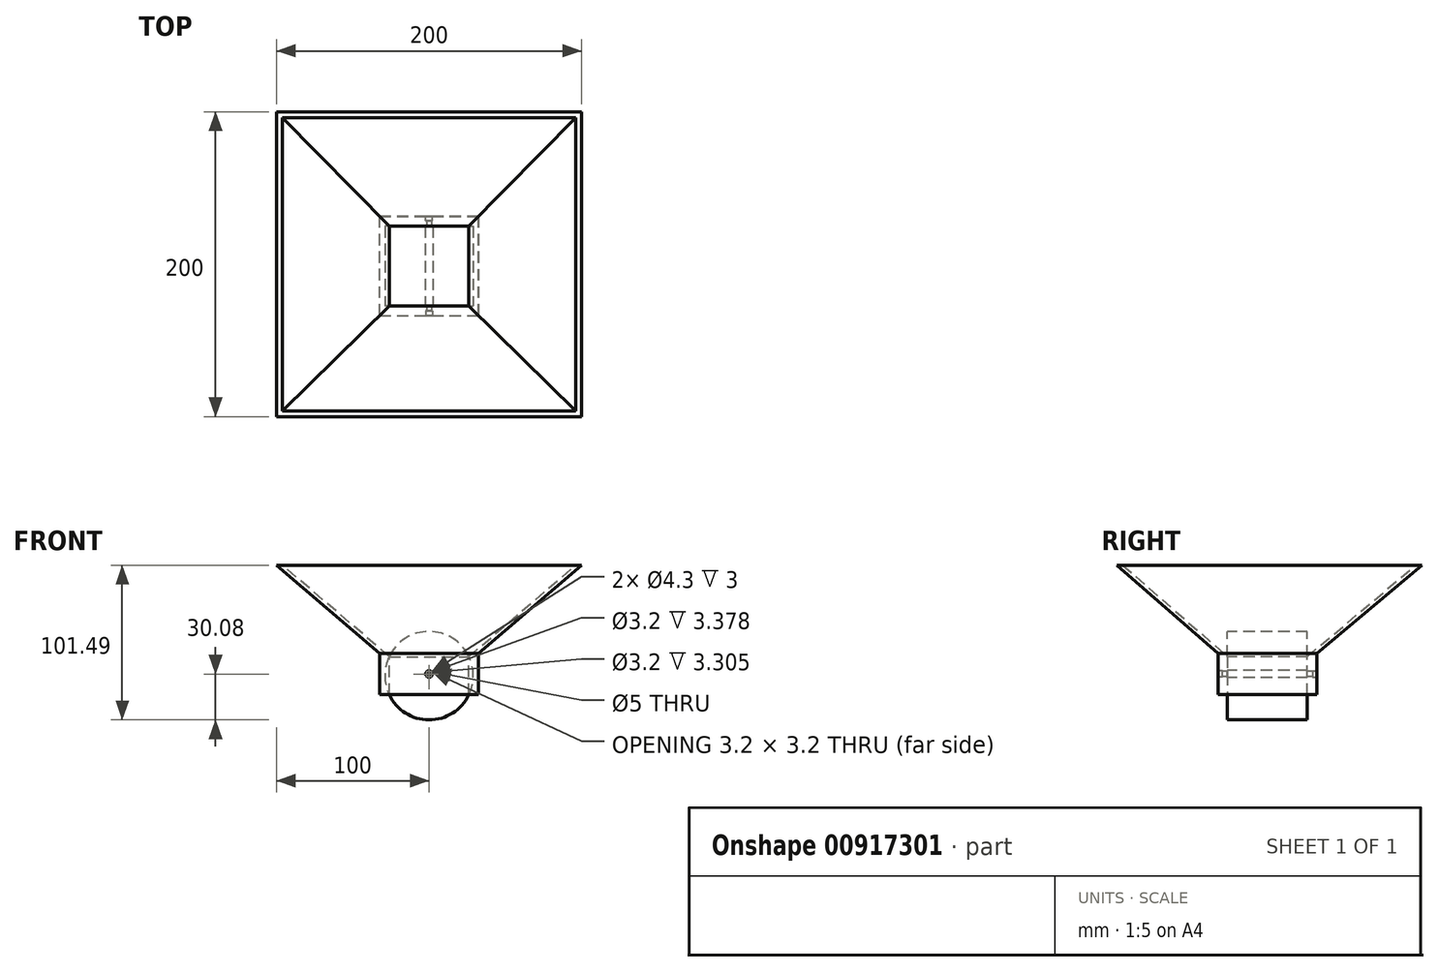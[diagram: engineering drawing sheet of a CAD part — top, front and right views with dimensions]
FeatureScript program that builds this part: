
annotation { "Feature Type Name" : "Feature", "Feature Type Description" : "" }
export const myFeature = defineFeature(function(context is Context, id is Id, definition is map)
    precondition{}
    {
        {
            assignVariable(context, id + "F0", {"name" : "top_height", "anyValue" : 60 * mm});
        }
        {
            var Q0;
            Q0=qCreatedBy(makeId("Top.planeOp"),FACE);
            var sketch = newSketch(context, id + "F1", { "sketchPlane" : qUnion([Q0])});
            skLineSegment(sketch, "E0.bottom", {"start": v(-100, 101.17) * mm, "end": v(100, 101.17) * mm});
            skLineSegment(sketch, "E0.top", {"start": v(-100, -98.83) * mm, "end": v(100, -98.83) * mm});
            skLineSegment(sketch, "E0.left", {"start": v(-100, 101.17) * mm, "end": v(-100, -98.83) * mm});
            skLineSegment(sketch, "E0.right", {"start": v(100, 101.17) * mm, "end": v(100, -98.83) * mm});
            skPoint(sketch, "E0.middle", {"position": v(0, 1.17) * mm});
            skSolve(sketch);
        }
        {
            var Q0;
            Q0=makeQuery(id+"F1.imprint","IMPRINT",FACE,{"disambiguationData":[TD([[makeQuery(id+"F1.imprint","IMPRINT",EDGE,{"derivedFrom":sQuery(id+"F1.wireOp",EDGE,"E0.bottom")}),-1.0]])]});
            cPlane(context, id + "F2", {"entities" : qUnion([Q0]), "cplaneType" : CPlaneType.OFFSET, "offset" : getVariable(context, 'top_height'), "oppositeDirection" : true, "width" : 150 * mm, "height" : 150 * mm});
        }
        {
            var Q0;
            Q0=qCreatedBy(id+"F2.planeOp",FACE);
            var sketch = newSketch(context, id + "F3", { "sketchPlane" : qUnion([Q0])});
            skLineSegment(sketch, "E1.bottom", {"start": v(30, 30) * mm, "end": v(-30, 30) * mm});
            skLineSegment(sketch, "E1.top", {"start": v(30, -30) * mm, "end": v(-30, -30) * mm});
            skLineSegment(sketch, "E1.left", {"start": v(30, 30) * mm, "end": v(30, -30) * mm});
            skLineSegment(sketch, "E1.right", {"start": v(-30, 30) * mm, "end": v(-30, -30) * mm});
            skPoint(sketch, "E1.middle", {"position": v(0, 0) * mm});
            skSolve(sketch);
        }
        {
            var Q0;
            Q0=makeQuery(id+"F1.imprint","IMPRINT",FACE,{"disambiguationData":[TD([[makeQuery(id+"F1.imprint","IMPRINT",EDGE,{"derivedFrom":sQuery(id+"F1.wireOp",EDGE,"E0.bottom")}),-1.0]])]});
            var Q1;
            Q1=makeQuery(id+"F3.imprint","IMPRINT",FACE,{"disambiguationData":[TD([[makeQuery(id+"F3.imprint","IMPRINT",EDGE,{"derivedFrom":sQuery(id+"F3.wireOp",EDGE,"E1.bottom")}),1.0]])]});
            loft(context, id + "F4", {"sheetProfilesArray" : [{ "sheetProfileEntities" : qUnion([Q0]) }, { "sheetProfileEntities" : qUnion([Q1]) }]});
        }
        {
            var Q0;
            Q0=makeQuery(id+"F4.opLoft","CAP_FACE",FACE,{"disambiguationData":[OSD([makeQuery(id+"F1.imprint","IMPRINT",FACE,{"disambiguationData":[TD([[makeQuery(id+"F1.imprint","IMPRINT",EDGE,{"derivedFrom":sQuery(id+"F1.wireOp",EDGE,"E0.bottom")}),-1.0]])]})])],"isStart":true});
            var Q1;
            Q1=makeQuery(id+"F4.opLoft","CAP_FACE",FACE,{"disambiguationData":[OSD([makeQuery(id+"F3.imprint","IMPRINT",FACE,{"disambiguationData":[TD([[makeQuery(id+"F3.imprint","IMPRINT",EDGE,{"derivedFrom":sQuery(id+"F3.wireOp",EDGE,"E1.bottom")}),1.0]])]})])],"isStart":true});
            shell(context, id + "F5", {"entities" : qUnion([Q0, Q1]), "thickness" : 2.5 * mm});
        }
        {
            var Q0;
            Q0=makeQuery(id+"F4.opLoft","CAP_FACE",FACE,{"disambiguationData":[OSD([makeQuery(id+"F3.imprint","IMPRINT",FACE,{"disambiguationData":[TD([[makeQuery(id+"F3.imprint","IMPRINT",EDGE,{"derivedFrom":sQuery(id+"F3.wireOp",EDGE,"E1.bottom")}),1.0]])]})])],"isStart":true});
            var sketch = newSketch(context, id + "F6", { "sketchPlane" : qUnion([Q0])});
            skLineSegment(sketch, "E2.bottom", {"start": v(-32.5, 32.5) * mm, "end": v(32.5, 32.5) * mm});
            skLineSegment(sketch, "E2.top", {"start": v(-32.5, -32.5) * mm, "end": v(32.5, -32.5) * mm});
            skLineSegment(sketch, "E2.left", {"start": v(-32.5, 32.5) * mm, "end": v(-32.5, -32.5) * mm});
            skLineSegment(sketch, "E2.right", {"start": v(32.5, 32.5) * mm, "end": v(32.5, -32.5) * mm});
            skPoint(sketch, "E2.middle", {"position": v(0, 0) * mm});
            skSolve(sketch);
        }
        {
            var Q0;
            Q0=makeQuery(id+"F6.imprint","IMPRINT",FACE,{"disambiguationData":[TD([[makeQuery(id+"F6.imprint","IMPRINT",EDGE,{"derivedFrom":sQuery(id+"F6.wireOp",EDGE,"E2.bottom")}),-1.0]])]});
            var Q1;
            {var subQ0=sQuery(id+"F3.wireOp",EDGE,"E1.right");var subQ1=sQuery(id+"F3.wireOp",EDGE,"E1.left");var subQ3=sQuery(id+"F3.wireOp",EDGE,"E1.bottom");Q1=makeQuery(id+"F6.imprint","IMPRINT",FACE,{"disambiguationData":[TD([[makeQuery(id+"F6.imprint","IMPRINT",EDGE,{"derivedFrom":makeQuery(id+"F4.opLoft","MID_CAP_EDGE",EDGE,{"disambiguationData":[OSD([subQ3,subQ1,subQ0])],"capPos":1.0})}),1.0]])]});}
            var Q2;
            Q2=makeQuery(id+"F4.opLoft","SWEPT_FACE",FACE,{"disambiguationData":[OSD([sQuery(id+"F1.wireOp",EDGE,"E0.bottom"),sQuery(id+"F1.wireOp",EDGE,"E0.top"),sQuery(id+"F1.wireOp",EDGE,"E0.left"),sQuery(id+"F3.wireOp",EDGE,"E1.bottom"),sQuery(id+"F3.wireOp",EDGE,"E1.top"),sQuery(id+"F3.wireOp",EDGE,"E1.right")])]});
            extrude(context, id + "F7", {"entities" : qUnion([Q0, Q1]), "operationType" : NewBodyOperationType.ADD, "depth" : 25 * mm, "offsetDistance" : 25 * mm, "hasSecondDirection" : true, "secondDirectionBound" : SecondDirectionBoundingType.UP_TO_NEXT, "secondDirectionOppositeDirection" : true, "secondDirectionDepth" : 25 * mm, "secondDirectionBoundEntityFace" : qUnion([Q2])});
        }
        {
            var Q0;
            Q0=makeQuery(id+"F7.opExtrude","SWEPT_FACE",FACE,{"disambiguationData":[OSD([sQuery(id+"F3.wireOp",EDGE,"E1.top"),sQuery(id+"F3.wireOp",EDGE,"E1.left"),sQuery(id+"F3.wireOp",EDGE,"E1.right")])]});
            var sketch = newSketch(context, id + "F8", { "sketchPlane" : qUnion([Q0])});
            skPoint(sketch, "E3", {"position": v(0, -85) * mm});
            skPoint(sketch, "E4", {"position": v(0, -60) * mm});
            skLineSegment(sketch, "E5", {"start": v(0, -85) * mm, "end": v(0, -60) * mm, "construction": true});
            skPoint(sketch, "E6", {"position": v(0, -72.5) * mm});
            skCircle(sketch, "E7", {"center": v(0, -72.5) * mm, "radius": 29 * mm});
            skSolve(sketch);
        }
        {
            var Q0;
            {var subQ1=sQuery(id+"F3.wireOp",EDGE,"E1.right");var subQ2=sQuery(id+"F3.wireOp",EDGE,"E1.left");var subQ3=sQuery(id+"F3.wireOp",EDGE,"E1.top");var subQ4=makeQuery(id+"F5.opShell","OFFSET_EDGE",EDGE,{"disambiguationData":[OSD([subQ3,subQ2,subQ1])]});var subQ5=makeQuery(id+"F7.opExtrude","CAP_EDGE",EDGE,{"disambiguationData":[OSD([subQ3,subQ2,subQ1]),TDD([makeQuery(id+"F6.imprint","IMPRINT",EDGE,{"derivedFrom":subQ4})])],"isStart":false});Q0=makeQuery(id+"F8.imprint","IMPRINT",FACE,{"disambiguationData":[TD([[makeQuery(id+"F8.imprint","IMPRINT",EDGE,{"derivedFrom":subQ5}),-1.0]])]});}
            var Q1;
            {var subQ0=sQuery(id+"F3.wireOp",EDGE,"E1.right");var subQ1=sQuery(id+"F3.wireOp",EDGE,"E1.left");var subQ2=sQuery(id+"F3.wireOp",EDGE,"E1.top");var subQ3=makeQuery(id+"F5.opShell","OFFSET_EDGE",EDGE,{"disambiguationData":[OSD([subQ2,subQ1,subQ0])]});var subQ5=makeQuery(id+"F6.imprint","IMPRINT",EDGE,{"derivedFrom":subQ3});Q1=makeQuery(id+"F8.imprint","IMPRINT",FACE,{"disambiguationData":[TD([[makeQuery(id+"F8.imprint","IMPRINT",EDGE,{"derivedFrom":makeQuery(id+"F7.opExtrude","CAP_EDGE",EDGE,{"disambiguationData":[OSD([subQ2,subQ1,subQ0]),TDD([subQ5])],"isStart":false})}),1.0]])]});}
            var Q2;
            {var subQ1=sQuery(id+"F3.wireOp",EDGE,"E1.right");var subQ2=sQuery(id+"F3.wireOp",EDGE,"E1.left");var subQ3=sQuery(id+"F3.wireOp",EDGE,"E1.top");var subQ4=makeQuery(id+"F5.opShell","OFFSET_EDGE",EDGE,{"disambiguationData":[OSD([subQ3,subQ2,subQ1])]});var subQ5=makeQuery(id+"F7.boolean.opBoolean","MERGE",EDGE,{"derivedFrom":[subQ4,makeQuery(id+"F7.opExtrude","CAP_EDGE",EDGE,{"disambiguationData":[OSD([subQ3,subQ2,subQ1]),TDD([subQ4,makeQuery(id+"F6.imprint","IMPRINT",EDGE,{"derivedFrom":subQ4})])],"isStart":false})]});Q2=makeQuery(id+"F8.imprint","IMPRINT",FACE,{"disambiguationData":[TD([[makeQuery(id+"F8.imprint","IMPRINT",EDGE,{"derivedFrom":subQ5}),1.0]])]});}
            var Q3;
            {var subQ1=sQuery(id+"F3.wireOp",EDGE,"E1.right");var subQ2=sQuery(id+"F3.wireOp",EDGE,"E1.left");var subQ3=sQuery(id+"F3.wireOp",EDGE,"E1.top");var subQ4=makeQuery(id+"F5.opShell","OFFSET_EDGE",EDGE,{"disambiguationData":[OSD([subQ3,subQ2,subQ1])]});var subQ6=sQuery(id+"F3.wireOp",EDGE,"E1.bottom");var subQ7=makeQuery(id+"F7.opExtrude","SWEPT_EDGE",EDGE,{"disambiguationData":[OSD([subQ6,subQ3,subQ2,subQ1]),TDD([makeQuery(id+"F6.imprint","INTERSECT",VERTEX,{"derivedFrom":[makeQuery(id+"F5.opShell","OFFSET_EDGE",EDGE,{"disambiguationData":[OSD([subQ6,subQ3,subQ1])]}),subQ4]})])]});Q3=makeQuery(id+"F8.imprint","IMPRINT",FACE,{"disambiguationData":[TD([[makeQuery(id+"F8.imprint","IMPRINT",EDGE,{"derivedFrom":subQ7}),-1.0]])]});}
            var Q4;
            {var subQ1=sQuery(id+"F3.wireOp",EDGE,"E1.right");var subQ2=sQuery(id+"F3.wireOp",EDGE,"E1.left");var subQ3=sQuery(id+"F3.wireOp",EDGE,"E1.top");var subQ4=makeQuery(id+"F5.opShell","OFFSET_EDGE",EDGE,{"disambiguationData":[OSD([subQ3,subQ2,subQ1])]});var subQ6=sQuery(id+"F3.wireOp",EDGE,"E1.bottom");var subQ7=makeQuery(id+"F7.opExtrude","SWEPT_EDGE",EDGE,{"disambiguationData":[OSD([subQ6,subQ3,subQ2,subQ1]),TDD([makeQuery(id+"F6.imprint","INTERSECT",VERTEX,{"derivedFrom":[makeQuery(id+"F5.opShell","OFFSET_EDGE",EDGE,{"disambiguationData":[OSD([subQ6,subQ3,subQ2])]}),subQ4]})])]});Q4=makeQuery(id+"F8.imprint","IMPRINT",FACE,{"disambiguationData":[TD([[makeQuery(id+"F8.imprint","IMPRINT",EDGE,{"derivedFrom":subQ7}),1.0]])]});}
            var Q5;
            Q5=makeQuery(id+"F7.opExtrude","SWEPT_FACE",FACE,{"disambiguationData":[OSD([sQuery(id+"F3.wireOp",EDGE,"E1.bottom"),sQuery(id+"F3.wireOp",EDGE,"E1.left"),sQuery(id+"F3.wireOp",EDGE,"E1.right")])]});
            extrude(context, id + "F9", {"entities" : qUnion([Q0, Q1, Q2, Q3, Q4]), "endBound" : BoundingType.UP_TO_SURFACE, "depth" : 25 * mm, "endBoundEntityFace" : qUnion([Q5]), "offsetDistance" : 25 * mm});
        }
        {
            var Q0;
            Q0=makeQuery(id+"F9.opExtrude","SWEPT_BODY",BODY,{"disambiguationData":[OSD([sQuery(id+"F8.wireOp",EDGE,"E7")])]});
            var Q1;
            Q1=makeQuery(id+"F4.opLoft","SWEPT_BODY",BODY,{"disambiguationData":[OSD([makeQuery(id+"F1.imprint","IMPRINT",FACE,{"disambiguationData":[TD([[makeQuery(id+"F1.imprint","IMPRINT",EDGE,{"derivedFrom":sQuery(id+"F1.wireOp",EDGE,"E0.bottom")}),-1.0]])]}),makeQuery(id+"F3.imprint","IMPRINT",FACE,{"disambiguationData":[TD([[makeQuery(id+"F3.imprint","IMPRINT",EDGE,{"derivedFrom":sQuery(id+"F3.wireOp",EDGE,"E1.bottom")}),1.0]])]})])]});
            booleanBodies(context, id + "F10", {"operationType" : BooleanOperationType.SUBTRACTION, "tools" : qUnion([Q0]), "targets" : qUnion([Q1]), "keepTools" : true});
        }
        {
            var Q0;
            Q0=makeQuery(id+"F9.opExtrude","CAP_FACE",FACE,{"disambiguationData":[OSD([sQuery(id+"F8.wireOp",EDGE,"E7")])],"isStart":true});
            var sketch = newSketch(context, id + "F11", { "sketchPlane" : qUnion([Q0])});
            skPoint(sketch, "E8", {"position": v(0, -57.82) * mm});
            skPoint(sketch, "E9", {"position": v(0, -85) * mm});
            skLineSegment(sketch, "E10", {"start": v(0, -57.82) * mm, "end": v(0, -85) * mm, "construction": true});
            skCircle(sketch, "E11", {"center": v(0, -71.41) * mm, "radius": 2.5 * mm});
            skSolve(sketch);
        }
        {
            var Q0;
            Q0=makeQuery(id+"F9.opExtrude","CAP_FACE",FACE,{"disambiguationData":[OSD([sQuery(id+"F8.wireOp",EDGE,"E7")])],"isStart":true});
            var sketch = newSketch(context, id + "F12", { "sketchPlane" : qUnion([Q0])});
            skCircle(sketch, "E12.0", {"center": v(0, -71.41) * mm, "radius": 2.5 * mm, "construction": true});
            skSolve(sketch);
        }
        {
            var Q0;
            Q0=makeQuery(id+"F11.imprint","IMPRINT",FACE,{"disambiguationData":[TD([[makeQuery(id+"F11.imprint","IMPRINT",EDGE,{"derivedFrom":sQuery(id+"F11.wireOp",EDGE,"E11")}),1.0]])]});
            extrude(context, id + "F13", {"entities" : qUnion([Q0]), "operationType" : NewBodyOperationType.REMOVE, "endBound" : BoundingType.UP_TO_NEXT, "oppositeDirection" : true, "depth" : 25 * mm, "offsetDistance" : 25 * mm});
        }
        {
            var Q0;
            Q0=makeQuery(id+"F7.opExtrude","SWEPT_FACE",FACE,{"disambiguationData":[OSD([sQuery(id+"F6.wireOp",EDGE,"E2.bottom")])]});
            var sketch = newSketch(context, id + "F14", { "sketchPlane" : qUnion([Q0])});
            skCircle(sketch, "E13.0", {"center": v(0, -71.41) * mm, "radius": 2.5 * mm, "construction": true});
            skSolve(sketch);
        }
        {
            var Q0;
            Q0=sQuery(id+"F14.wireOp",VERTEX,"E13.0.center");
            var Q1;
            Q1=makeQuery(id+"F4.opLoft","SWEPT_BODY",BODY,{"disambiguationData":[OSD([makeQuery(id+"F1.imprint","IMPRINT",FACE,{"disambiguationData":[TD([[makeQuery(id+"F1.imprint","IMPRINT",EDGE,{"derivedFrom":sQuery(id+"F1.wireOp",EDGE,"E0.bottom")}),-1.0]])]}),makeQuery(id+"F3.imprint","IMPRINT",FACE,{"disambiguationData":[TD([[makeQuery(id+"F3.imprint","IMPRINT",EDGE,{"derivedFrom":sQuery(id+"F3.wireOp",EDGE,"E1.bottom")}),1.0]])]})])]});
            hole(context, id + "F15", {"style" : HoleStyle.C_BORE, "endStyle" : HoleEndStyle.THROUGH, "holeDiameter" : 3.2 * mm, "cBoreDiameter" : 4.3 * mm, "cBoreDepth" : 3 * mm, "majorDiameter" : 5 * mm, "isTappedThrough" : true, "tappedDepth" : 1.27 * mm, "tapClearance" : 3, "locations" : qUnion([Q0]), "scope" : qUnion([Q1])});
        }
        {
            var Q0;
            Q0=makeQuery(id+"F7.opExtrude","SWEPT_FACE",FACE,{"disambiguationData":[OSD([sQuery(id+"F6.wireOp",EDGE,"E2.top")])]});
            var sketch = newSketch(context, id + "F16", { "sketchPlane" : qUnion([Q0])});
            skCircle(sketch, "E14.0", {"center": v(0, -71.41) * mm, "radius": 1.6 * mm});
            skSolve(sketch);
        }
        {
            var Q0;
            Q0=sQuery(id+"F16.wireOp",VERTEX,"E14.0.center");
            var Q1;
            Q1=makeQuery(id+"F4.opLoft","SWEPT_BODY",BODY,{"disambiguationData":[OSD([makeQuery(id+"F1.imprint","IMPRINT",FACE,{"disambiguationData":[TD([[makeQuery(id+"F1.imprint","IMPRINT",EDGE,{"derivedFrom":sQuery(id+"F1.wireOp",EDGE,"E0.bottom")}),-1.0]])]}),makeQuery(id+"F3.imprint","IMPRINT",FACE,{"disambiguationData":[TD([[makeQuery(id+"F3.imprint","IMPRINT",EDGE,{"derivedFrom":sQuery(id+"F3.wireOp",EDGE,"E1.bottom")}),1.0]])]})])]});
            hole(context, id + "F17", {"style" : HoleStyle.C_BORE, "endStyle" : HoleEndStyle.THROUGH, "holeDiameter" : 3.2 * mm, "cBoreDiameter" : 4.3 * mm, "cBoreDepth" : 3 * mm, "majorDiameter" : 5 * mm, "isTappedThrough" : true, "tappedDepth" : 1.27 * mm, "tapClearance" : 3, "locations" : qUnion([Q0]), "scope" : qUnion([Q1])});
        }
        {
            var Q0;
            Q0=sQuery(id+"F12.wireOp",VERTEX,"E12.0.center");
            var Q1;
            Q1=makeQuery(id+"F9.opExtrude","SWEPT_FACE",FACE,{"disambiguationData":[OSD([sQuery(id+"F8.wireOp",EDGE,"E7")])]});
            cPlane(context, id + "F18", {"entities" : qUnion([Q0, Q1]), "cplaneType" : CPlaneType.LINE_ANGLE, "offset" : 25 * mm, "angle" : 0 * degree, "oppositeDirection" : true, "width" : 150 * mm, "height" : 150 * mm});
        }
        {
            var Q0;
            Q0=makeQuery(id+"F12.imprint","IMPRINT",FACE,{"disambiguationData":[TD([[makeQuery(id+"F12.imprint","IMPRINT",EDGE,{"derivedFrom":makeQuery(id+"F9.opExtrude","CAP_EDGE",EDGE,{"disambiguationData":[OSD([sQuery(id+"F8.wireOp",EDGE,"E7")])],"isStart":true})}),-1.0]])]});
            var sketch = newSketch(context, id + "F19", { "sketchPlane" : qUnion([Q0])});
            skCircle(sketch, "E15.0", {"center": v(0, -71.41) * mm, "radius": 2.5 * mm, "construction": true});
            skCircle(sketch, "E16.0", {"center": v(0, -72.5) * mm, "radius": 29 * mm});
            skLineSegment(sketch, "E17", {"start": v(0, -71.41) * mm, "end": v(28.97, -71.41) * mm, "construction": true});
            skSolve(sketch);
        }
        {
            var Q0;
            Q0=makeQuery(id+"F12.imprint","IMPRINT",FACE,{"disambiguationData":[TD([[makeQuery(id+"F12.imprint","IMPRINT",EDGE,{"derivedFrom":makeQuery(id+"F9.opExtrude","CAP_EDGE",EDGE,{"disambiguationData":[OSD([sQuery(id+"F8.wireOp",EDGE,"E7")])],"isStart":true})}),-1.0]])]});
            var sketch = newSketch(context, id + "F20", { "sketchPlane" : qUnion([Q0])});
            skCircle(sketch, "E18.0", {"center": v(0, -72.5) * mm, "radius": 29 * mm});
            skLineSegment(sketch, "E19.0", {"start": v(-96.16, 0) * mm, "end": v(-26.16, -60) * mm, "construction": true});
            skLineSegment(sketch, "E20", {"start": v(-26.16, -60) * mm, "end": v(-26.16, -85) * mm});
            skLineSegment(sketch, "E21.0", {"start": v(96.16, 0) * mm, "end": v(26.16, -60) * mm, "construction": true});
            skLineSegment(sketch, "E22", {"start": v(26.16, -60) * mm, "end": v(26.16, -85) * mm});
            skSolve(sketch);
        }
        {
            var Q0;
            {var subQ0=sQuery(id+"F20.wireOp",EDGE,"E20");Q0=makeQuery(id+"F20.imprint","IMPRINT",FACE,{"disambiguationData":[TD([[makeQuery(id+"F20.imprint","IMPRINT",EDGE,{"derivedFrom":subQ0}),-1.0]])]});}
            var Q1;
            {var subQ0=sQuery(id+"F20.wireOp",EDGE,"E22");Q1=makeQuery(id+"F20.imprint","IMPRINT",FACE,{"disambiguationData":[TD([[makeQuery(id+"F20.imprint","IMPRINT",EDGE,{"derivedFrom":subQ0}),1.0]])]});}
            extrude(context, id + "F21", {"entities" : qUnion([Q0, Q1]), "operationType" : NewBodyOperationType.REMOVE, "endBound" : BoundingType.UP_TO_NEXT, "oppositeDirection" : true, "depth" : 25 * mm, "offsetDistance" : 25 * mm});
        }
    });
